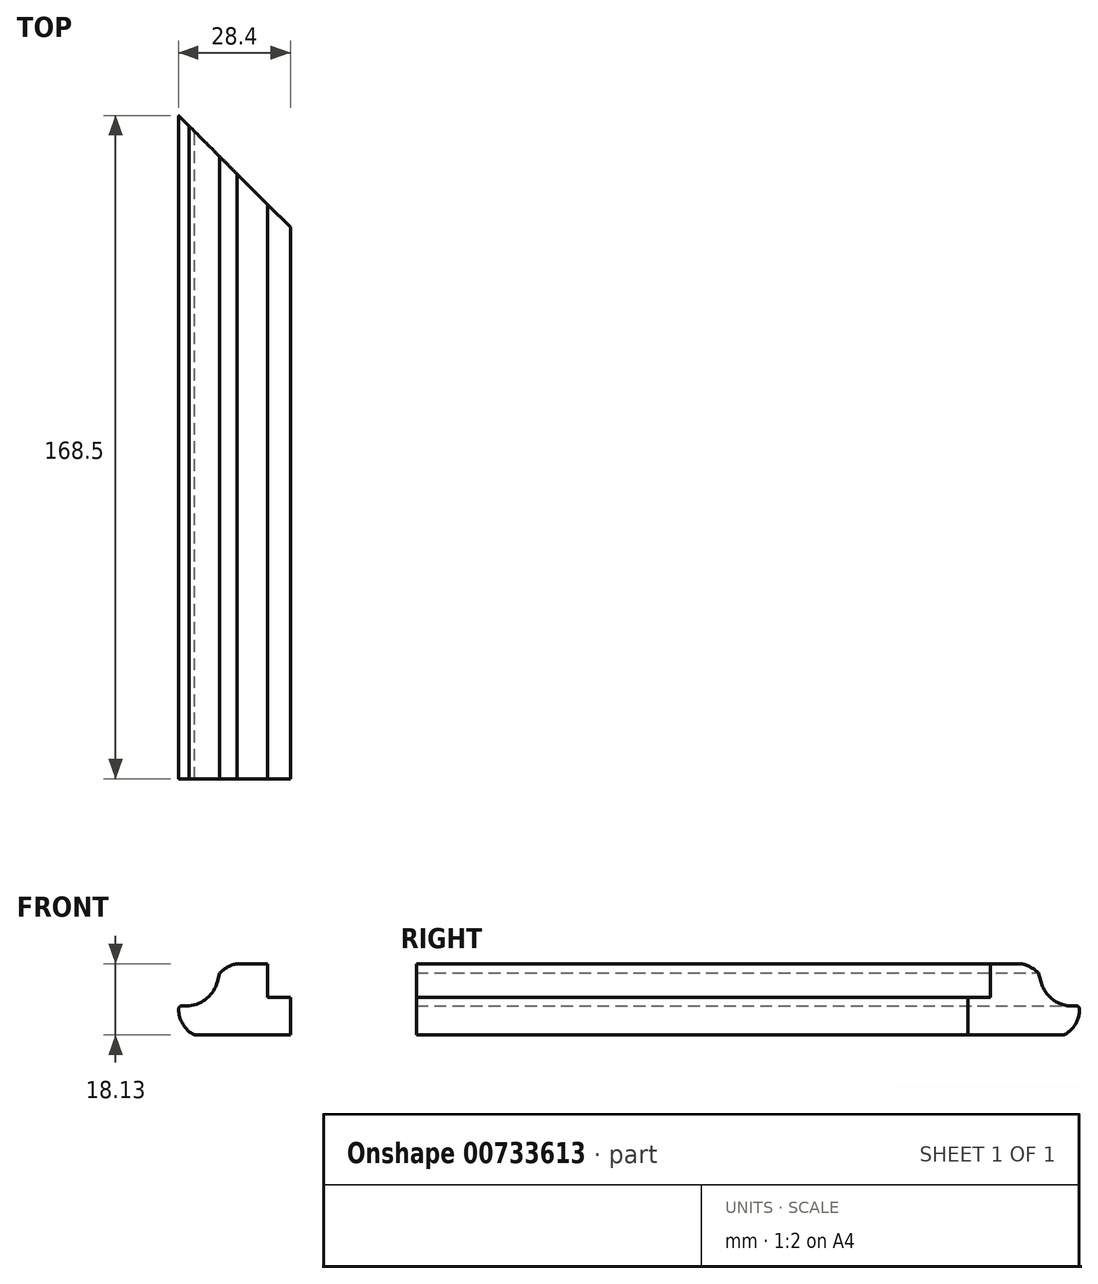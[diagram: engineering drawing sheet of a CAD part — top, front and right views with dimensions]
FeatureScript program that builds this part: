
annotation { "Feature Type Name" : "Feature", "Feature Type Description" : "" }
export const myFeature = defineFeature(function(context is Context, id is Id, definition is map)
    precondition{}
    {
        {
            var Q0;
            Q0=qCreatedBy(makeId("Front.planeOp"),FACE);
            var sketch = newSketch(context, id + "F0", { "sketchPlane" : qUnion([Q0])});
            skLineSegment(sketch, "E0", {"start": v(-24.4, 0) * mm, "end": v(0, 0) * mm});
            skLineSegment(sketch, "E1", {"start": v(0, 0) * mm, "end": v(0, 9.63) * mm});
            skLineSegment(sketch, "E2", {"start": v(0, 9.63) * mm, "end": v(-5.8, 9.63) * mm});
            skLineSegment(sketch, "E3", {"start": v(-5.8, 9.63) * mm, "end": v(-5.8, 18.13) * mm});
            skLineSegment(sketch, "E4", {"start": v(-5.8, 18.13) * mm, "end": v(-13.53, 18.13) * mm});
            skPoint(sketch, "E5", {"position": v(-28.4, 6.59) * mm});
            skArc(sketch, "E6", {"start": v(-25.76, 7.39) * mm, "mid": v(-21.16, 9.38) * mm, "end": v(-18.5, 13.63) * mm});
            skLineSegment(sketch, "E7", {"start": v(-18.5, 13.63) * mm, "end": v(-17.95, 15.75) * mm});
            skArc(sketch, "E8", {"start": v(-13.53, 18.13) * mm, "mid": v(-15.92, 17.28) * mm, "end": v(-17.95, 15.75) * mm});
            skArc(sketch, "E9", {"start": v(-27.6, 7.39) * mm, "mid": v(-28.17, 7.16) * mm, "end": v(-28.4, 6.59) * mm});
            skArc(sketch, "E10", {"start": v(-28.4, 6.59) * mm, "mid": v(-27.32, 2.74) * mm, "end": v(-24.4, 0) * mm});
            skLineSegment(sketch, "E11", {"start": v(-27.6, 7.39) * mm, "end": v(-25.76, 7.39) * mm});
            skSolve(sketch);
        }
        {
            var Q0;
            Q0 = qSketchRegion(id + "F0", true);
            extrude(context, id + "F1", {"entities" : qUnion([Q0]), "depth" : 168.5 * mm, "offsetDistance" : 25 * mm});
        }
        {
            var Q0;
            Q0=qCreatedBy(makeId("Top.planeOp"),FACE);
            var sketch = newSketch(context, id + "F2", { "sketchPlane" : qUnion([Q0])});
            skPoint(sketch, "E12.0", {"position": v(-28.4, 0) * mm});
            skLineSegment(sketch, "E13", {"start": v(-28.4, 0) * mm, "end": v(0, 0) * mm});
            skLineSegment(sketch, "E14", {"start": v(0, 0) * mm, "end": v(0, -28.4) * mm});
            skLineSegment(sketch, "E15", {"start": v(0, -28.4) * mm, "end": v(-28.4, 0) * mm});
            skPoint(sketch, "E16", {"position": v(-13.42, 8.6) * mm});
            skLineSegment(sketch, "E17.0", {"start": v(-5.8, -168.5) * mm, "end": v(-5.8, 0) * mm});
            skPoint(sketch, "E18", {"position": v(-5.8, -22.6) * mm});
            skSolve(sketch);
        }
        {
            var Q0;
            Q0 = qSketchRegion(id + "F2", true);
            extrude(context, id + "F3", {"entities" : qUnion([Q0]), "operationType" : NewBodyOperationType.REMOVE, "depth" : 25 * mm, "offsetDistance" : 25 * mm});
        }
    });
